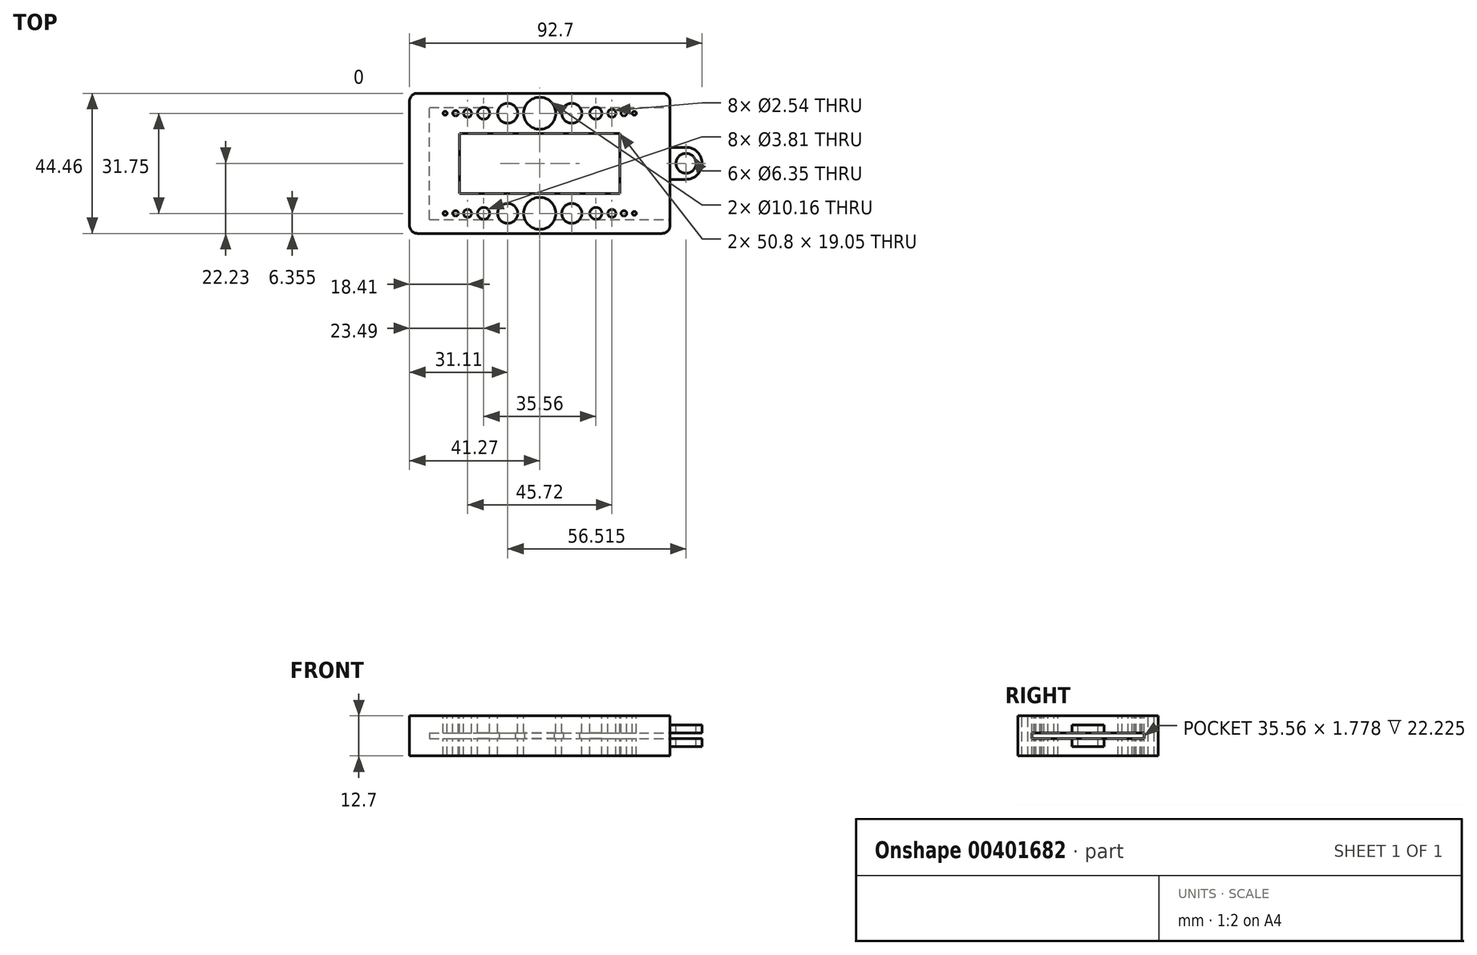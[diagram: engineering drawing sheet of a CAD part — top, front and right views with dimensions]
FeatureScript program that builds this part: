
annotation { "Feature Type Name" : "Feature", "Feature Type Description" : "" }
export const myFeature = defineFeature(function(context is Context, id is Id, definition is map)
    precondition{}
    {
        {
            var Q0;
            Q0=qCreatedBy(makeId("Top.planeOp"),FACE);
            var sketch = newSketch(context, id + "F0", { "sketchPlane" : qUnion([Q0])});
            skLineSegment(sketch, "E0.bottom", {"start": v(-38.74, 22.23) * mm, "end": v(38.74, 22.23) * mm});
            skLineSegment(sketch, "E0.top", {"start": v(-38.74, -22.23) * mm, "end": v(38.74, -22.23) * mm});
            skLineSegment(sketch, "E0.left", {"start": v(-41.28, 19.69) * mm, "end": v(-41.28, -19.69) * mm});
            skLineSegment(sketch, "E0.right", {"start": v(41.28, 19.69) * mm, "end": v(41.28, -19.69) * mm});
            skPoint(sketch, "E0.middle", {"position": v(0, 0) * mm});
            skPoint(sketch, "E1.visualSharp", {"position": v(-41.28, 22.23) * mm});
            skArc(sketch, "E1.filletArc", {"start": v(-38.74, 22.23) * mm, "mid": v(-40.53, 21.48) * mm, "end": v(-41.28, 19.69) * mm});
            skPoint(sketch, "E2.visualSharp", {"position": v(41.28, 22.23) * mm});
            skArc(sketch, "E2.filletArc", {"start": v(41.28, 19.69) * mm, "mid": v(40.53, 21.48) * mm, "end": v(38.74, 22.23) * mm});
            skPoint(sketch, "E3.visualSharp", {"position": v(41.28, -22.23) * mm});
            skArc(sketch, "E3.filletArc", {"start": v(38.74, -22.23) * mm, "mid": v(40.53, -21.48) * mm, "end": v(41.28, -19.69) * mm});
            skPoint(sketch, "E4.visualSharp", {"position": v(-41.28, -22.23) * mm});
            skArc(sketch, "E4.filletArc", {"start": v(-41.28, -19.69) * mm, "mid": v(-40.53, -21.48) * mm, "end": v(-38.74, -22.23) * mm});
            skSolve(sketch);
        }
        {
            var Q0;
            Q0 = qSketchRegion(id + "F0", true);
            extrude(context, id + "F1", {"entities" : qUnion([Q0]), "endBound" : BoundingType.SYMMETRIC, "depth" : 12.7 * mm});
        }
        {
            var Q0;
            Q0=makeQuery(id+"F1.opExtrude","CAP_FACE",FACE,{"disambiguationData":[OSD([sQuery(id+"F0.wireOp",EDGE,"E0.bottom"),sQuery(id+"F0.wireOp",EDGE,"E0.top"),sQuery(id+"F0.wireOp",EDGE,"E0.left"),sQuery(id+"F0.wireOp",EDGE,"E0.right"),sQuery(id+"F0.wireOp",EDGE,"E1.filletArc"),sQuery(id+"F0.wireOp",EDGE,"E2.filletArc"),sQuery(id+"F0.wireOp",EDGE,"E3.filletArc"),sQuery(id+"F0.wireOp",EDGE,"E4.filletArc")])],"isStart":false});
            var sketch = newSketch(context, id + "F2", { "sketchPlane" : qUnion([Q0])});
            skLineSegment(sketch, "E5.bottom", {"start": v(-25.4, 9.53) * mm, "end": v(25.4, 9.53) * mm});
            skLineSegment(sketch, "E5.top", {"start": v(-25.4, -9.53) * mm, "end": v(25.4, -9.53) * mm});
            skLineSegment(sketch, "E5.left", {"start": v(-25.4, 9.53) * mm, "end": v(-25.4, -9.53) * mm});
            skLineSegment(sketch, "E5.right", {"start": v(25.4, 9.53) * mm, "end": v(25.4, -9.53) * mm});
            skPoint(sketch, "E5.middle", {"position": v(0, 0) * mm});
            skLineSegment(sketch, "E6", {"start": v(0, 22.23) * mm, "end": v(0, 9.53) * mm, "construction": true});
            skLineSegment(sketch, "E7", {"start": v(0, -9.53) * mm, "end": v(0, -22.23) * mm, "construction": true});
            skLineSegment(sketch, "E8", {"start": v(-25.4, 0) * mm, "end": v(-41.28, 0) * mm, "construction": true});
            skCircle(sketch, "E9", {"center": v(0, 15.88) * mm, "radius": 5.08 * mm});
            skCircle(sketch, "E10", {"center": v(-10.16, 15.88) * mm, "radius": 3.18 * mm});
            skCircle(sketch, "E11", {"center": v(-29.97, 15.88) * mm, "radius": 0.64 * mm});
            skCircle(sketch, "E12", {"center": v(-17.78, 15.88) * mm, "radius": 1.9 * mm});
            skCircle(sketch, "E13", {"center": v(-22.86, 15.88) * mm, "radius": 1.27 * mm});
            skCircle(sketch, "E14", {"center": v(-26.67, 15.88) * mm, "radius": 0.89 * mm});
            skLineSegment(sketch, "E15", {"start": v(0, 15.88) * mm, "end": v(-41.28, 15.88) * mm, "construction": true});
            skCircle(sketch, "E16.MirrorC", {"center": v(29.97, 15.88) * mm, "radius": 0.64 * mm});
            skCircle(sketch, "E17.MirrorC", {"center": v(22.86, 15.88) * mm, "radius": 1.27 * mm});
            skCircle(sketch, "E18.MirrorC", {"center": v(26.67, 15.88) * mm, "radius": 0.89 * mm});
            skLineSegment(sketch, "E19.MirrorCS", {"start": v(0, 15.88) * mm, "end": v(41.28, 15.88) * mm, "construction": true});
            skCircle(sketch, "E20.MirrorC", {"center": v(17.78, 15.88) * mm, "radius": 1.9 * mm});
            skCircle(sketch, "E21.MirrorC", {"center": v(10.16, 15.88) * mm, "radius": 3.18 * mm});
            skCircle(sketch, "E22.MirrorC", {"center": v(29.97, -15.88) * mm, "radius": 0.64 * mm});
            skCircle(sketch, "E23.MirrorC", {"center": v(0, -15.87) * mm, "radius": 5.08 * mm});
            skCircle(sketch, "E24.MirrorC", {"center": v(26.67, -15.88) * mm, "radius": 0.89 * mm});
            skLineSegment(sketch, "E25.MirrorCS", {"start": v(0, -15.88) * mm, "end": v(41.28, -15.87) * mm, "construction": true});
            skCircle(sketch, "E26.MirrorC", {"center": v(-22.86, -15.88) * mm, "radius": 1.27 * mm});
            skCircle(sketch, "E27.MirrorC", {"center": v(-29.97, -15.88) * mm, "radius": 0.64 * mm});
            skLineSegment(sketch, "E28.MirrorCS", {"start": v(0, -15.88) * mm, "end": v(-41.28, -15.88) * mm, "construction": true});
            skCircle(sketch, "E29.MirrorC", {"center": v(22.86, -15.88) * mm, "radius": 1.27 * mm});
            skCircle(sketch, "E30.MirrorC", {"center": v(17.78, -15.88) * mm, "radius": 1.9 * mm});
            skCircle(sketch, "E31.MirrorC", {"center": v(-26.67, -15.88) * mm, "radius": 0.89 * mm});
            skCircle(sketch, "E32.MirrorC", {"center": v(-10.16, -15.88) * mm, "radius": 3.18 * mm});
            skCircle(sketch, "E33.MirrorC", {"center": v(10.16, -15.87) * mm, "radius": 3.18 * mm});
            skLineSegment(sketch, "E34.MirrorCS", {"start": v(0, -22.22) * mm, "end": v(0, -9.52) * mm, "construction": true});
            skCircle(sketch, "E35.MirrorC", {"center": v(-17.78, -15.88) * mm, "radius": 1.9 * mm});
            skSolve(sketch);
        }
        {
            var Q0;
            Q0 = qSketchRegion(id + "F2", true);
            extrude(context, id + "F3", {"entities" : qUnion([Q0]), "operationType" : NewBodyOperationType.REMOVE, "endBound" : BoundingType.UP_TO_NEXT, "oppositeDirection" : true, "depth" : 25.4 * mm});
        }
        {
            var Q0;
            Q0=makeQuery(id+"F1.opExtrude","SWEPT_FACE",FACE,{"disambiguationData":[OSD([sQuery(id+"F0.wireOp",EDGE,"E0.right")])]});
            var sketch = newSketch(context, id + "F4", { "sketchPlane" : qUnion([Q0])});
            skLineSegment(sketch, "E36.bottom", {"start": v(-17.78, 0.89) * mm, "end": v(17.78, 0.89) * mm});
            skLineSegment(sketch, "E36.top", {"start": v(-17.78, -0.89) * mm, "end": v(17.78, -0.89) * mm});
            skLineSegment(sketch, "E36.left", {"start": v(-17.78, 0.89) * mm, "end": v(-17.78, -0.89) * mm});
            skLineSegment(sketch, "E36.right", {"start": v(17.78, 0.89) * mm, "end": v(17.78, -0.89) * mm});
            skPoint(sketch, "E36.middle", {"position": v(0, 0) * mm});
            skSolve(sketch);
        }
        {
            var Q0;
            Q0 = qSketchRegion(id + "F4", true);
            extrude(context, id + "F5", {"entities" : qUnion([Q0]), "operationType" : NewBodyOperationType.REMOVE, "oppositeDirection" : true, "depth" : 76.2 * mm});
        }
        {
            var Q0;
            Q0=makeQuery(id+"F1.opExtrude","SWEPT_FACE",FACE,{"disambiguationData":[OSD([sQuery(id+"F0.wireOp",EDGE,"E0.right")])]});
            var sketch = newSketch(context, id + "F6", { "sketchPlane" : qUnion([Q0])});
            skLineSegment(sketch, "E37.bottom", {"start": v(-5.08, 0.89) * mm, "end": v(5.08, 0.89) * mm});
            skLineSegment(sketch, "E37.top", {"start": v(-5.08, 3.43) * mm, "end": v(5.08, 3.43) * mm});
            skLineSegment(sketch, "E37.left", {"start": v(-5.08, 0.89) * mm, "end": v(-5.08, 3.43) * mm});
            skLineSegment(sketch, "E37.right", {"start": v(5.08, 0.89) * mm, "end": v(5.08, 3.43) * mm});
            skPoint(sketch, "E37.middle", {"position": v(0, 2.16) * mm});
            skLineSegment(sketch, "E38.bottom", {"start": v(5.08, -0.89) * mm, "end": v(-5.08, -0.89) * mm});
            skLineSegment(sketch, "E38.top", {"start": v(5.08, -3.43) * mm, "end": v(-5.08, -3.43) * mm});
            skLineSegment(sketch, "E38.left", {"start": v(5.08, -0.89) * mm, "end": v(5.08, -3.43) * mm});
            skLineSegment(sketch, "E38.right", {"start": v(-5.08, -0.89) * mm, "end": v(-5.08, -3.43) * mm});
            skPoint(sketch, "E38.middle", {"position": v(0, -2.16) * mm});
            skSolve(sketch);
        }
        {
            var Q0;
            Q0 = qSketchRegion(id + "F6", true);
            extrude(context, id + "F7", {"entities" : qUnion([Q0]), "operationType" : NewBodyOperationType.ADD, "depth" : 10.16 * mm});
        }
        {
            var Q0;
            Q0=makeQuery(id+"F7.opExtrude","CAP_EDGE",EDGE,{"disambiguationData":[OSD([sQuery(id+"F6.wireOp",EDGE,"E37.left")])],"isStart":false});
            var Q1;
            Q1=makeQuery(id+"F7.opExtrude","CAP_EDGE",EDGE,{"disambiguationData":[OSD([sQuery(id+"F6.wireOp",EDGE,"E37.right")])],"isStart":false});
            var Q2;
            Q2=makeQuery(id+"F7.opExtrude","CAP_EDGE",EDGE,{"disambiguationData":[OSD([sQuery(id+"F6.wireOp",EDGE,"E38.left")])],"isStart":false});
            var Q3;
            Q3=makeQuery(id+"F7.opExtrude","CAP_EDGE",EDGE,{"disambiguationData":[OSD([sQuery(id+"F6.wireOp",EDGE,"E38.right")])],"isStart":false});
            var Q4;
            Q4=makeQuery(id+"F7.opExtrude","CAP_EDGE",EDGE,{"disambiguationData":[OSD([sQuery(id+"F6.wireOp",EDGE,"E37.left")])],"isStart":true});
            var Q5;
            Q5=makeQuery(id+"F7.opExtrude","CAP_EDGE",EDGE,{"disambiguationData":[OSD([sQuery(id+"F6.wireOp",EDGE,"E38.right")])],"isStart":true});
            var Q6;
            Q6=makeQuery(id+"F7.opExtrude","CAP_EDGE",EDGE,{"disambiguationData":[OSD([sQuery(id+"F6.wireOp",EDGE,"E37.right")])],"isStart":true});
            var Q7;
            Q7=makeQuery(id+"F7.opExtrude","CAP_EDGE",EDGE,{"disambiguationData":[OSD([sQuery(id+"F6.wireOp",EDGE,"E38.left")])],"isStart":true});
            fillet(context, id + "F8", {"entities" : qUnion([Q0, Q1, Q2, Q3, Q4, Q5, Q6, Q7]), "radius" : 5.08 * mm, "tangentPropagation" : true, "allowEdgeOverflow" : false});
        }
        {
            var Q0;
            Q0=makeQuery(id+"F7.opExtrude","SWEPT_FACE",FACE,{"disambiguationData":[OSD([sQuery(id+"F6.wireOp",EDGE,"E37.top")])]});
            var sketch = newSketch(context, id + "F9", { "sketchPlane" : qUnion([Q0])});
            skCircle(sketch, "E39", {"center": v(46.36, 0) * mm, "radius": 3.18 * mm});
            skSolve(sketch);
        }
        {
            var Q0;
            Q0 = qSketchRegion(id + "F9", true);
            extrude(context, id + "F10", {"entities" : qUnion([Q0]), "operationType" : NewBodyOperationType.REMOVE, "oppositeDirection" : true, "depth" : 25.4 * mm});
        }
    });
